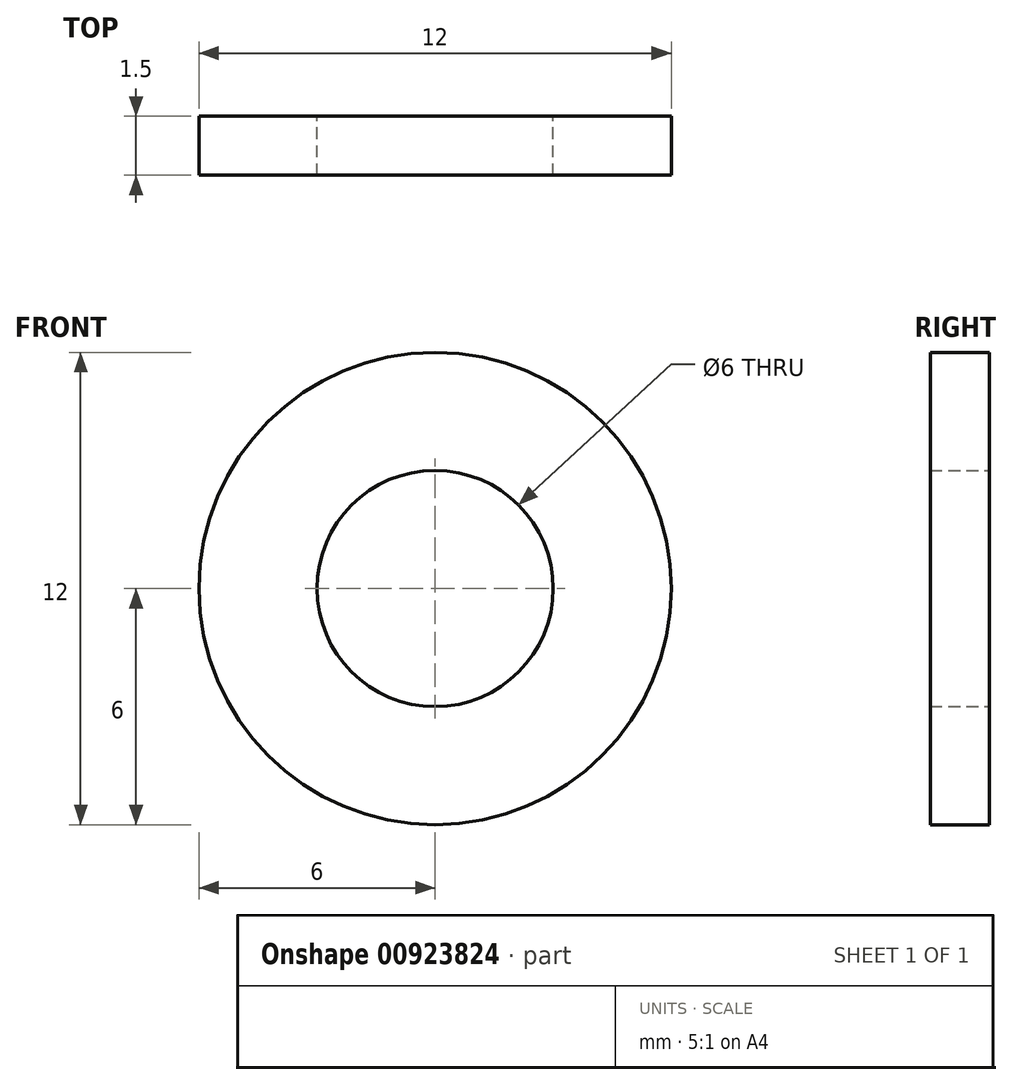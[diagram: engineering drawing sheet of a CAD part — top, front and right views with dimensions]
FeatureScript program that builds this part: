
annotation { "Feature Type Name" : "Feature", "Feature Type Description" : "" }
export const myFeature = defineFeature(function(context is Context, id is Id, definition is map)
    precondition{}
    {
        {
            var Q0;
            Q0=qCreatedBy(makeId("Front.planeOp"),FACE);
            var sketch = newSketch(context, id + "F0", { "sketchPlane" : qUnion([Q0])});
            skCircle(sketch, "E0", {"center": v(0, 0) * mm, "radius": 3 * mm});
            skCircle(sketch, "E1", {"center": v(0, 0) * mm, "radius": 6 * mm});
            skSolve(sketch);
        }
        {
            var Q0;
            Q0=makeQuery(id+"F0.imprint","IMPRINT",FACE,{"disambiguationData":[TD([[makeQuery(id+"F0.imprint","IMPRINT",EDGE,{"derivedFrom":sQuery(id+"F0.wireOp",EDGE,"E0")}),-1.0]])]});
            extrude(context, id + "F1", {"entities" : qUnion([Q0]), "depth" : 1.5 * mm, "offsetDistance" : 25 * mm});
        }
    });
